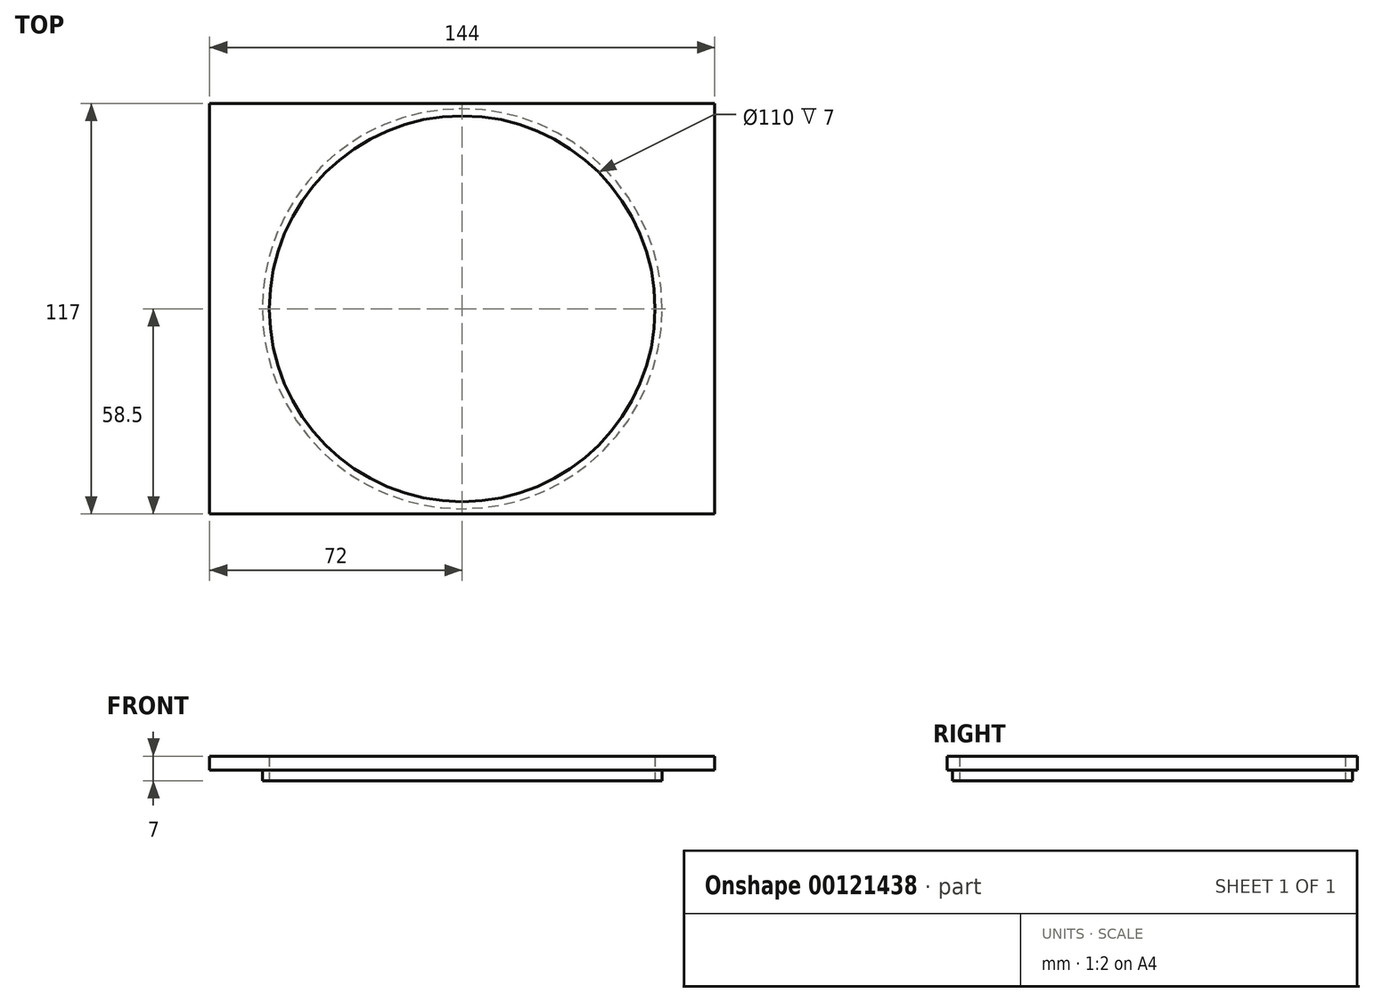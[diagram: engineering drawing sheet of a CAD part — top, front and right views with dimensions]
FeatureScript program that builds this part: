
annotation { "Feature Type Name" : "Feature", "Feature Type Description" : "" }
export const myFeature = defineFeature(function(context is Context, id is Id, definition is map)
    precondition{}
    {
        {
            var Q0;
            Q0=qCreatedBy(makeId("Top.planeOp"),FACE);
            var sketch = newSketch(context, id + "F0", { "sketchPlane" : qUnion([Q0])});
            skLineSegment(sketch, "E0.bottom", {"start": v(-72, 58.5) * mm, "end": v(72, 58.5) * mm});
            skLineSegment(sketch, "E0.top", {"start": v(-72, -58.5) * mm, "end": v(72, -58.5) * mm});
            skLineSegment(sketch, "E0.left", {"start": v(-72, 58.5) * mm, "end": v(-72, -58.5) * mm});
            skLineSegment(sketch, "E0.right", {"start": v(72, 58.5) * mm, "end": v(72, -58.5) * mm});
            skCircle(sketch, "E1", {"center": v(0, 0) * mm, "radius": 55 * mm});
            skSolve(sketch);
        }
        {
            var Q0;
            Q0 = qSketchRegion(id + "F0", true);
            extrude(context, id + "F1", {"entities" : qUnion([Q0]), "depth" : 4 * mm});
        }
        {
            var Q0;
            Q0=makeQuery(id+"F1.opExtrude","CAP_FACE",FACE,{"disambiguationData":[OSD([sQuery(id+"F0.wireOp",EDGE,"E0.bottom"),sQuery(id+"F0.wireOp",EDGE,"E0.top"),sQuery(id+"F0.wireOp",EDGE,"E0.left"),sQuery(id+"F0.wireOp",EDGE,"E0.right"),sQuery(id+"F0.wireOp",EDGE,"E1")])],"isStart":true});
            var sketch = newSketch(context, id + "F2", { "sketchPlane" : qUnion([Q0])});
            skCircle(sketch, "E2", {"center": v(0, 0) * mm, "radius": 55 * mm});
            skCircle(sketch, "E3", {"center": v(0, 0) * mm, "radius": 57 * mm});
            skSolve(sketch);
        }
        {
            var Q0;
            Q0 = qSketchRegion(id + "F2", true);
            extrude(context, id + "F3", {"entities" : qUnion([Q0]), "operationType" : NewBodyOperationType.ADD, "depth" : 3 * mm});
        }
    });
